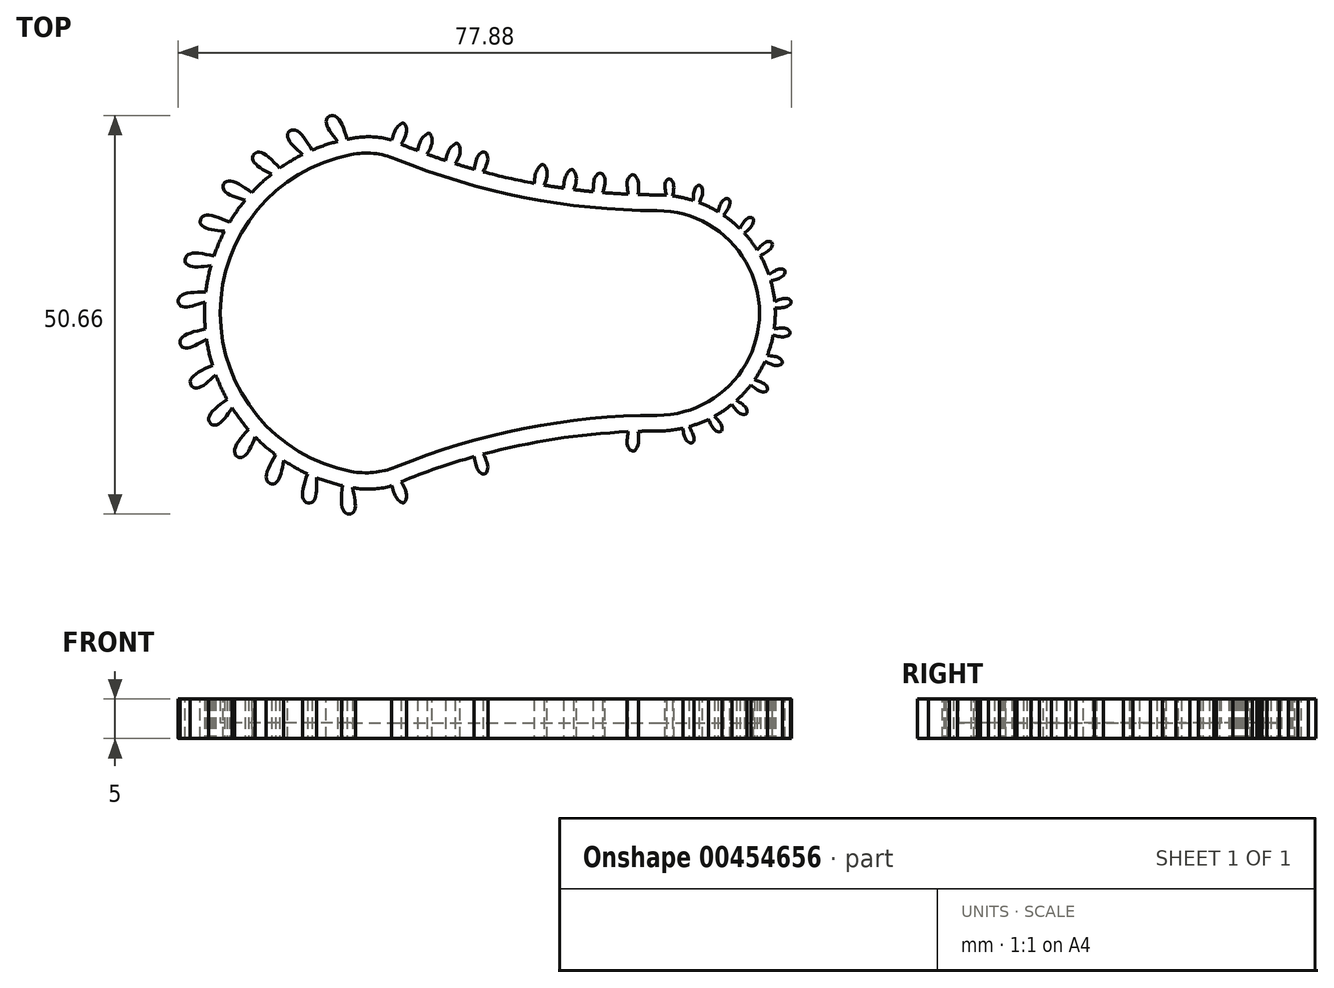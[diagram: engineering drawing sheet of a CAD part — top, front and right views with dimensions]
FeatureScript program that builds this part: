
annotation { "Feature Type Name" : "Feature", "Feature Type Description" : "" }
export const myFeature = defineFeature(function(context is Context, id is Id, definition is map)
    precondition{}
    {
        {
            var Q0;
            Q0=qCreatedBy(makeId("Top.planeOp"),FACE);
            var sketch = newSketch(context, id + "F0", { "sketchPlane" : qUnion([Q0])});
            skArc(sketch, "E0", {"start": v(35, -15) * mm, "mid": v(50, 0) * mm, "end": v(35, 15) * mm});
            skArc(sketch, "E1", {"start": v(0, 22.5) * mm, "mid": v(17.1, 16.92) * mm, "end": v(35, 15) * mm});
            skLineSegment(sketch, "E2", {"start": v(-44.1, 0) * mm, "end": v(67.74, 0) * mm, "construction": true});
            skArc(sketch, "E3.MirrorCS", {"start": v(0, -22.5) * mm, "mid": v(17.1, -16.92) * mm, "end": v(35, -15) * mm});
            skArc(sketch, "E4.trimOffspring", {"start": v(0, 22.5) * mm, "mid": v(-22.5, 0) * mm, "end": v(0, -22.5) * mm});
            skFitSpline(sketch, "E5", {"points": [v(-10.03, 20.14) * mm, v(-11.85, 22.05) * mm, v(-11.83, 22.96) * mm, v(-10.89, 23.2) * mm, v(-8.86, 20.68) * mm], "startDerivative": vector(-7.63, 6.57) * mm, "endDerivative": vector(6.03, -10.27) * mm});
            skArc(sketch, "E6.0", {"start": v(-0.41, 20.5) * mm, "mid": v(16.9, 14.92) * mm, "end": v(35, 13) * mm});
            skArc(sketch, "E6.1", {"start": v(-0.41, 20.5) * mm, "mid": v(-20.5, 0) * mm, "end": v(-0.41, -20.5) * mm});
            skArc(sketch, "E6.2", {"start": v(-0.41, -20.5) * mm, "mid": v(16.9, -14.92) * mm, "end": v(35, -13) * mm});
            skArc(sketch, "E6.3", {"start": v(35, -13) * mm, "mid": v(48, 0) * mm, "end": v(35, 13) * mm});
            skFitSpline(sketch, "E7", {"points": [v(1.28, 21.94) * mm, v(1.73, 23.23) * mm, v(2.29, 23.91) * mm, v(2.81, 24.12) * mm, v(3.13, 23.02) * mm, v(2.48, 21.44) * mm], "startDerivative": vector(1.7, 6.07) * mm, "endDerivative": vector(-3.53, -5.81) * mm});
            skFitSpline(sketch, "E8.MirrorCS", {"points": [v(1.28, -21.94) * mm, v(1.73, -23.23) * mm, v(2.29, -23.91) * mm, v(2.81, -24.12) * mm, v(3.13, -23.02) * mm, v(2.48, -21.44) * mm], "startDerivative": vector(1.7, -6.07) * mm, "endDerivative": vector(-3.53, 5.81) * mm});
            skFitSpline(sketch, "E9", {"points": [v(36.16, 14.96) * mm, v(36, 15.88) * mm, v(36.08, 16.62) * mm, v(36.47, 17.02) * mm, v(36.96, 16.66) * mm, v(37.1, 15.76) * mm, v(36.96, 14.87) * mm], "startDerivative": vector(-1.08, 5.15) * mm, "endDerivative": vector(-0.96, -4.87) * mm});
            skFitSpline(sketch, "E10", {"points": [v(4.54, 20.63) * mm, v(4.99, 21.91) * mm, v(5.54, 22.6) * mm, v(6.07, 22.8) * mm, v(6.4, 21.71) * mm, v(5.74, 20.13) * mm], "startDerivative": vector(1.7, 6.07) * mm, "endDerivative": vector(-3.53, -5.81) * mm});
            skFitSpline(sketch, "E11", {"points": [v(8.1, 19.37) * mm, v(8.55, 20.65) * mm, v(9.1, 21.34) * mm, v(9.63, 21.54) * mm, v(9.95, 20.45) * mm, v(9.3, 18.87) * mm], "startDerivative": vector(1.7, 6.07) * mm, "endDerivative": vector(-3.53, -5.81) * mm});
            skFitSpline(sketch, "E12", {"points": [v(11.75, 18.25) * mm, v(12.06, 19.58) * mm, v(12.56, 20.3) * mm, v(13.17, 20.4) * mm, v(13.48, 19.5) * mm, v(12.9, 17.93) * mm], "startDerivative": vector(1.17, 6.2) * mm, "endDerivative": vector(-3, -6.1) * mm});
            skFitSpline(sketch, "E13", {"points": [v(15.92, 17.18) * mm, v(16.14, 18.53) * mm, v(16.57, 19.3) * mm, v(17.05, 19.6) * mm, v(17.56, 18.57) * mm, v(17.19, 16.9) * mm], "startDerivative": vector(0.63, 6.27) * mm, "endDerivative": vector(-2.46, -6.34) * mm});
            skFitSpline(sketch, "E14", {"points": [v(19.36, 16.46) * mm, v(19.58, 17.8) * mm, v(20, 18.57) * mm, v(20.5, 18.86) * mm, v(21, 17.84) * mm, v(20.62, 16.17) * mm], "startDerivative": vector(0.63, 6.27) * mm, "endDerivative": vector(-2.46, -6.34) * mm});
            skFitSpline(sketch, "E15", {"points": [v(23.08, 15.83) * mm, v(23.3, 17.17) * mm, v(23.73, 17.95) * mm, v(24.21, 18.24) * mm, v(24.72, 17.22) * mm, v(24.35, 15.54) * mm], "startDerivative": vector(0.63, 6.27) * mm, "endDerivative": vector(-2.46, -6.34) * mm});
            skFitSpline(sketch, "E16", {"points": [v(26.87, 15.36) * mm, v(26.95, 16.72) * mm, v(27.31, 17.53) * mm, v(27.9, 17.74) * mm, v(28.36, 16.9) * mm, v(28.07, 15.25) * mm], "startDerivative": vector(0.08, 6.3) * mm, "endDerivative": vector(-1.9, -6.53) * mm});
            skFitSpline(sketch, "E17", {"points": [v(31.3, 15.09) * mm, v(31.17, 16.46) * mm, v(31.46, 17.29) * mm, v(32.02, 17.55) * mm, v(32.56, 16.74) * mm, v(32.55, 15.04) * mm], "startDerivative": vector(-0.47, 6.29) * mm, "endDerivative": vector(-1.32, -6.67) * mm});
            skFitSpline(sketch, "E18.MirrorCS", {"points": [v(4.54, -20.63) * mm, v(4.99, -21.91) * mm, v(5.54, -22.6) * mm, v(6.07, -22.8) * mm, v(6.4, -21.71) * mm, v(5.74, -20.13) * mm], "startDerivative": vector(1.7, -6.07) * mm, "endDerivative": vector(-3.53, 5.81) * mm});
            skFitSpline(sketch, "E19.MirrorCS", {"points": [v(8.1, -19.37) * mm, v(8.55, -20.65) * mm, v(9.1, -21.34) * mm, v(9.63, -21.54) * mm, v(9.95, -20.45) * mm, v(9.3, -18.87) * mm], "startDerivative": vector(1.7, -6.07) * mm, "endDerivative": vector(-3.53, 5.81) * mm});
            skFitSpline(sketch, "E20.MirrorCS", {"points": [v(15.92, -17.18) * mm, v(16.14, -18.53) * mm, v(16.57, -19.3) * mm, v(17.05, -19.6) * mm, v(17.56, -18.57) * mm, v(17.19, -16.9) * mm], "startDerivative": vector(0.63, -6.27) * mm, "endDerivative": vector(-2.46, 6.34) * mm});
            skFitSpline(sketch, "E21.MirrorCS", {"points": [v(19.36, -16.46) * mm, v(19.58, -17.8) * mm, v(20, -18.57) * mm, v(20.5, -18.86) * mm, v(21, -17.84) * mm, v(20.62, -16.17) * mm], "startDerivative": vector(0.63, -6.27) * mm, "endDerivative": vector(-2.46, 6.34) * mm});
            skFitSpline(sketch, "E22.MirrorCS", {"points": [v(23.08, -15.83) * mm, v(23.3, -17.17) * mm, v(23.73, -17.95) * mm, v(24.21, -18.24) * mm, v(24.72, -17.22) * mm, v(24.35, -15.54) * mm], "startDerivative": vector(0.63, -6.27) * mm, "endDerivative": vector(-2.46, 6.34) * mm});
            skFitSpline(sketch, "E23.MirrorCS", {"points": [v(26.87, -15.36) * mm, v(26.95, -16.72) * mm, v(27.31, -17.53) * mm, v(27.9, -17.74) * mm, v(28.36, -16.9) * mm, v(28.07, -15.25) * mm], "startDerivative": vector(0.08, -6.3) * mm, "endDerivative": vector(-1.9, 6.53) * mm});
            skFitSpline(sketch, "E24.MirrorCS", {"points": [v(31.3, -15.09) * mm, v(31.17, -16.46) * mm, v(31.46, -17.29) * mm, v(32.02, -17.55) * mm, v(32.56, -16.74) * mm, v(32.55, -15.04) * mm], "startDerivative": vector(-0.47, -6.29) * mm, "endDerivative": vector(-1.32, 6.67) * mm});
            skFitSpline(sketch, "E25.MirrorCS", {"points": [v(11.75, -18.25) * mm, v(12.06, -19.58) * mm, v(12.56, -20.3) * mm, v(13.17, -20.4) * mm, v(13.48, -19.5) * mm, v(12.9, -17.93) * mm], "startDerivative": vector(1.17, -6.2) * mm, "endDerivative": vector(-3, 6.1) * mm});
            skSolve(sketch);
        }
        {
            var Q0;
            Q0=makeQuery(id+"F0.imprint","IMPRINT",FACE,{"disambiguationData":[TD([[makeQuery(id+"F0.imprint","IMPRINT",EDGE,{"derivedFrom":sQuery(id+"F0.wireOp",EDGE,"E6.0")}),-1.0]])]});
            extrude(context, id + "F1", {"entities" : qUnion([Q0]), "depth" : 2 * mm});
        }
        {
            var Q0;
            Q0=makeQuery(id+"F0.imprint","IMPRINT",FACE,{"disambiguationData":[TD([[makeQuery(id+"F0.imprint","IMPRINT",EDGE,{"derivedFrom":sQuery(id+"F0.wireOp",EDGE,"E0")}),1.0]])]});
            var Q1;
            {var subQ0=sQuery(id+"F0.wireOp",EDGE,"E5");Q1=makeQuery(id+"F0.imprint","IMPRINT",FACE,{"disambiguationData":[TD([[makeQuery(id+"F0.imprint","IMPRINT",EDGE,{"derivedFrom":subQ0}),-1.0]])]});}
            var Q2;
            {var subQ0=sQuery(id+"F0.wireOp",EDGE,"E7");Q2=makeQuery(id+"F0.imprint","IMPRINT",FACE,{"disambiguationData":[TD([[makeQuery(id+"F0.imprint","IMPRINT",EDGE,{"derivedFrom":subQ0}),-1.0]])]});}
            var Q3;
            {var subQ0=sQuery(id+"F0.wireOp",EDGE,"E9");Q3=makeQuery(id+"F0.imprint","IMPRINT",FACE,{"disambiguationData":[TD([[makeQuery(id+"F0.imprint","IMPRINT",EDGE,{"derivedFrom":subQ0}),-1.0]])]});}
            var Q4;
            {var subQ0=sQuery(id+"F0.wireOp",EDGE,"E8.MirrorCS");Q4=makeQuery(id+"F0.imprint","IMPRINT",FACE,{"disambiguationData":[TD([[makeQuery(id+"F0.imprint","IMPRINT",EDGE,{"derivedFrom":subQ0}),1.0]])]});}
            var Q5;
            {var subQ0=sQuery(id+"F0.wireOp",EDGE,"E10");var subQ1=sQuery(id+"F0.wireOp",EDGE,"E1");var subQ2=makeQuery(id+"F0.imprint","INTERSECT",VERTEX,{"disambiguationData":[OD(0.0)],"derivedFrom":[subQ1,subQ0]});Q5=makeQuery(id+"F0.imprint","IMPRINT",FACE,{"disambiguationData":[TD([[makeQuery(id+"F0.imprint","IMPRINT",EDGE,{"disambiguationData":[TD([[subQ2,-1.0]])],"derivedFrom":subQ1}),1.0]])]});}
            var Q6;
            {var subQ0=sQuery(id+"F0.wireOp",EDGE,"E11");var subQ1=sQuery(id+"F0.wireOp",EDGE,"E1");var subQ2=makeQuery(id+"F0.imprint","INTERSECT",VERTEX,{"disambiguationData":[OD(0.0)],"derivedFrom":[subQ1,subQ0]});Q6=makeQuery(id+"F0.imprint","IMPRINT",FACE,{"disambiguationData":[TD([[makeQuery(id+"F0.imprint","IMPRINT",EDGE,{"disambiguationData":[TD([[subQ2,-1.0]])],"derivedFrom":subQ1}),1.0]])]});}
            var Q7;
            {var subQ0=sQuery(id+"F0.wireOp",EDGE,"E12");Q7=makeQuery(id+"F0.imprint","IMPRINT",FACE,{"disambiguationData":[TD([[makeQuery(id+"F0.imprint","IMPRINT",EDGE,{"derivedFrom":subQ0}),-1.0]])]});}
            var Q8;
            {var subQ0=sQuery(id+"F0.wireOp",EDGE,"E13");var subQ1=sQuery(id+"F0.wireOp",EDGE,"E1");var subQ2=makeQuery(id+"F0.imprint","INTERSECT",VERTEX,{"disambiguationData":[OD(0.0)],"derivedFrom":[subQ1,subQ0]});Q8=makeQuery(id+"F0.imprint","IMPRINT",FACE,{"disambiguationData":[TD([[makeQuery(id+"F0.imprint","IMPRINT",EDGE,{"disambiguationData":[TD([[subQ2,-1.0]])],"derivedFrom":subQ1}),1.0]])]});}
            var Q9;
            {var subQ0=sQuery(id+"F0.wireOp",EDGE,"E14");var subQ1=sQuery(id+"F0.wireOp",EDGE,"E1");var subQ2=makeQuery(id+"F0.imprint","INTERSECT",VERTEX,{"disambiguationData":[OD(0.0)],"derivedFrom":[subQ1,subQ0]});Q9=makeQuery(id+"F0.imprint","IMPRINT",FACE,{"disambiguationData":[TD([[makeQuery(id+"F0.imprint","IMPRINT",EDGE,{"disambiguationData":[TD([[subQ2,-1.0]])],"derivedFrom":subQ1}),1.0]])]});}
            var Q10;
            {var subQ0=sQuery(id+"F0.wireOp",EDGE,"E15");var subQ1=sQuery(id+"F0.wireOp",EDGE,"E1");var subQ2=makeQuery(id+"F0.imprint","INTERSECT",VERTEX,{"disambiguationData":[OD(0.0)],"derivedFrom":[subQ1,subQ0]});Q10=makeQuery(id+"F0.imprint","IMPRINT",FACE,{"disambiguationData":[TD([[makeQuery(id+"F0.imprint","IMPRINT",EDGE,{"disambiguationData":[TD([[subQ2,-1.0]])],"derivedFrom":subQ1}),1.0]])]});}
            var Q11;
            {var subQ0=sQuery(id+"F0.wireOp",EDGE,"E16");var subQ1=sQuery(id+"F0.wireOp",EDGE,"E1");var subQ2=makeQuery(id+"F0.imprint","INTERSECT",VERTEX,{"disambiguationData":[OD(0.0)],"derivedFrom":[subQ1,subQ0]});Q11=makeQuery(id+"F0.imprint","IMPRINT",FACE,{"disambiguationData":[TD([[makeQuery(id+"F0.imprint","IMPRINT",EDGE,{"disambiguationData":[TD([[subQ2,-1.0]])],"derivedFrom":subQ1}),1.0]])]});}
            var Q12;
            {var subQ0=sQuery(id+"F0.wireOp",EDGE,"E18.MirrorCS");var subQ1=sQuery(id+"F0.wireOp",EDGE,"E3.MirrorCS");var subQ2=makeQuery(id+"F0.imprint","INTERSECT",VERTEX,{"disambiguationData":[OD(0.0)],"derivedFrom":[subQ1,subQ0]});Q12=makeQuery(id+"F0.imprint","IMPRINT",FACE,{"disambiguationData":[TD([[makeQuery(id+"F0.imprint","IMPRINT",EDGE,{"disambiguationData":[TD([[subQ2,-1.0]])],"derivedFrom":subQ1}),-1.0]])]});}
            var Q13;
            {var subQ0=sQuery(id+"F0.wireOp",EDGE,"E19.MirrorCS");var subQ1=sQuery(id+"F0.wireOp",EDGE,"E3.MirrorCS");var subQ2=makeQuery(id+"F0.imprint","INTERSECT",VERTEX,{"disambiguationData":[OD(0.0)],"derivedFrom":[subQ1,subQ0]});Q13=makeQuery(id+"F0.imprint","IMPRINT",FACE,{"disambiguationData":[TD([[makeQuery(id+"F0.imprint","IMPRINT",EDGE,{"disambiguationData":[TD([[subQ2,-1.0]])],"derivedFrom":subQ1}),-1.0]])]});}
            var Q14;
            {var subQ0=sQuery(id+"F0.wireOp",EDGE,"E25.MirrorCS");Q14=makeQuery(id+"F0.imprint","IMPRINT",FACE,{"disambiguationData":[TD([[makeQuery(id+"F0.imprint","IMPRINT",EDGE,{"derivedFrom":subQ0}),1.0]])]});}
            var Q15;
            {var subQ0=sQuery(id+"F0.wireOp",EDGE,"E20.MirrorCS");var subQ1=sQuery(id+"F0.wireOp",EDGE,"E3.MirrorCS");var subQ2=makeQuery(id+"F0.imprint","INTERSECT",VERTEX,{"disambiguationData":[OD(0.0)],"derivedFrom":[subQ1,subQ0]});Q15=makeQuery(id+"F0.imprint","IMPRINT",FACE,{"disambiguationData":[TD([[makeQuery(id+"F0.imprint","IMPRINT",EDGE,{"disambiguationData":[TD([[subQ2,-1.0]])],"derivedFrom":subQ1}),-1.0]])]});}
            var Q16;
            {var subQ0=sQuery(id+"F0.wireOp",EDGE,"E21.MirrorCS");var subQ1=sQuery(id+"F0.wireOp",EDGE,"E3.MirrorCS");var subQ2=makeQuery(id+"F0.imprint","INTERSECT",VERTEX,{"disambiguationData":[OD(0.0)],"derivedFrom":[subQ1,subQ0]});Q16=makeQuery(id+"F0.imprint","IMPRINT",FACE,{"disambiguationData":[TD([[makeQuery(id+"F0.imprint","IMPRINT",EDGE,{"disambiguationData":[TD([[subQ2,-1.0]])],"derivedFrom":subQ1}),-1.0]])]});}
            var Q17;
            {var subQ0=sQuery(id+"F0.wireOp",EDGE,"E22.MirrorCS");var subQ1=sQuery(id+"F0.wireOp",EDGE,"E3.MirrorCS");var subQ2=makeQuery(id+"F0.imprint","INTERSECT",VERTEX,{"disambiguationData":[OD(0.0)],"derivedFrom":[subQ1,subQ0]});Q17=makeQuery(id+"F0.imprint","IMPRINT",FACE,{"disambiguationData":[TD([[makeQuery(id+"F0.imprint","IMPRINT",EDGE,{"disambiguationData":[TD([[subQ2,-1.0]])],"derivedFrom":subQ1}),-1.0]])]});}
            var Q18;
            {var subQ0=sQuery(id+"F0.wireOp",EDGE,"E23.MirrorCS");var subQ1=sQuery(id+"F0.wireOp",EDGE,"E3.MirrorCS");var subQ2=makeQuery(id+"F0.imprint","INTERSECT",VERTEX,{"disambiguationData":[OD(0.0)],"derivedFrom":[subQ1,subQ0]});Q18=makeQuery(id+"F0.imprint","IMPRINT",FACE,{"disambiguationData":[TD([[makeQuery(id+"F0.imprint","IMPRINT",EDGE,{"disambiguationData":[TD([[subQ2,-1.0]])],"derivedFrom":subQ1}),-1.0]])]});}
            var Q19;
            {var subQ0=sQuery(id+"F0.wireOp",EDGE,"E24.MirrorCS");Q19=makeQuery(id+"F0.imprint","IMPRINT",FACE,{"disambiguationData":[TD([[makeQuery(id+"F0.imprint","IMPRINT",EDGE,{"derivedFrom":subQ0}),1.0]])]});}
            var Q20;
            {var subQ0=sQuery(id+"F0.wireOp",EDGE,"E17");Q20=makeQuery(id+"F0.imprint","IMPRINT",FACE,{"disambiguationData":[TD([[makeQuery(id+"F0.imprint","IMPRINT",EDGE,{"derivedFrom":subQ0}),-1.0]])]});}
            extrude(context, id + "F2", {"entities" : qUnion([Q0, Q1, Q2, Q3, Q4, Q5, Q6, Q7, Q8, Q9, Q10, Q11, Q12, Q13, Q14, Q15, Q16, Q17, Q18, Q19, Q20]), "operationType" : NewBodyOperationType.ADD, "depth" : 5 * mm});
        }
        {
            var Q0;
            Q0=makeQuery(id+"F2.opExtrude","SWEPT_EDGE",EDGE,{"disambiguationData":[OSD([sQuery(id+"F0.wireOp",EDGE,"E1"),sQuery(id+"F0.wireOp",EDGE,"E4.trimOffspring")])]});
            var Q1;
            Q1=makeQuery(id+"F2.opExtrude","SWEPT_EDGE",EDGE,{"disambiguationData":[OSD([sQuery(id+"F0.wireOp",EDGE,"E3.MirrorCS"),sQuery(id+"F0.wireOp",EDGE,"E4.trimOffspring")])]});
            var Q2;
            Q2=makeQuery(id+"F2.opExtrude","SWEPT_EDGE",EDGE,{"disambiguationData":[OSD([sQuery(id+"F0.wireOp",EDGE,"E6.0"),sQuery(id+"F0.wireOp",EDGE,"E6.1")])]});
            var Q3;
            Q3=makeQuery(id+"F2.opExtrude","SWEPT_EDGE",EDGE,{"disambiguationData":[OSD([sQuery(id+"F0.wireOp",EDGE,"E6.1"),sQuery(id+"F0.wireOp",EDGE,"E6.2")])]});
            fillet(context, id + "F3", {"entities" : qUnion([Q0, Q1, Q2, Q3]), "radius" : 10 * mm, "tangentPropagation" : true, "allowEdgeOverflow" : false});
        }
        {
            var Q0;
            Q0=makeQuery(id+"F2.opExtrude","SWEPT_FACE",FACE,{"disambiguationData":[OSD([sQuery(id+"F0.wireOp",EDGE,"E5")])]});
            var Q1;
            {var subQ0=sQuery(id+"F0.wireOp",EDGE,"E4.trimOffspring");Q1=makeQuery(id+"F2.opExtrude","CAP_EDGE",EDGE,{"disambiguationData":[OSD([subQ0]),TDD([makeQuery(id+"F0.imprint","IMPRINT",EDGE,{"disambiguationData":[TD([[makeQuery(id+"F0.imprint","INTERSECT",VERTEX,{"derivedFrom":[sQuery(id+"F0.wireOp",EDGE,"E3.MirrorCS"),subQ0]}),1.0]])],"derivedFrom":subQ0})])],"isStart":false});}
            circularPattern(context, id + "F4", {"patternType" : PatternType.FACE, "faces" : qUnion([Q0]), "axis" : qUnion([Q1]), "angle" : 360 * degree, "instanceCount" : 30, "equalSpace" : true});
        }
        {
            var Q0;
            Q0=makeQuery(id+"F2.opExtrude","SWEPT_FACE",FACE,{"disambiguationData":[OSD([sQuery(id+"F0.wireOp",EDGE,"E9")])]});
            var Q1;
            {var subQ0=sQuery(id+"F0.wireOp",EDGE,"E0");Q1=makeQuery(id+"F2.opExtrude","SWEPT_FACE",FACE,{"disambiguationData":[OSD([subQ0]),TDD([makeQuery(id+"F0.imprint","IMPRINT",EDGE,{"disambiguationData":[TD([[makeQuery(id+"F0.imprint","INTERSECT",VERTEX,{"derivedFrom":[subQ0,sQuery(id+"F0.wireOp",EDGE,"E3.MirrorCS")]}),-1.0]])],"derivedFrom":subQ0})])]});}
            circularPattern(context, id + "F5", {"patternType" : PatternType.FACE, "faces" : qUnion([Q0]), "axis" : qUnion([Q1]), "angle" : 360 * degree, "instanceCount" : 27, "equalSpace" : true});
        }
    });
